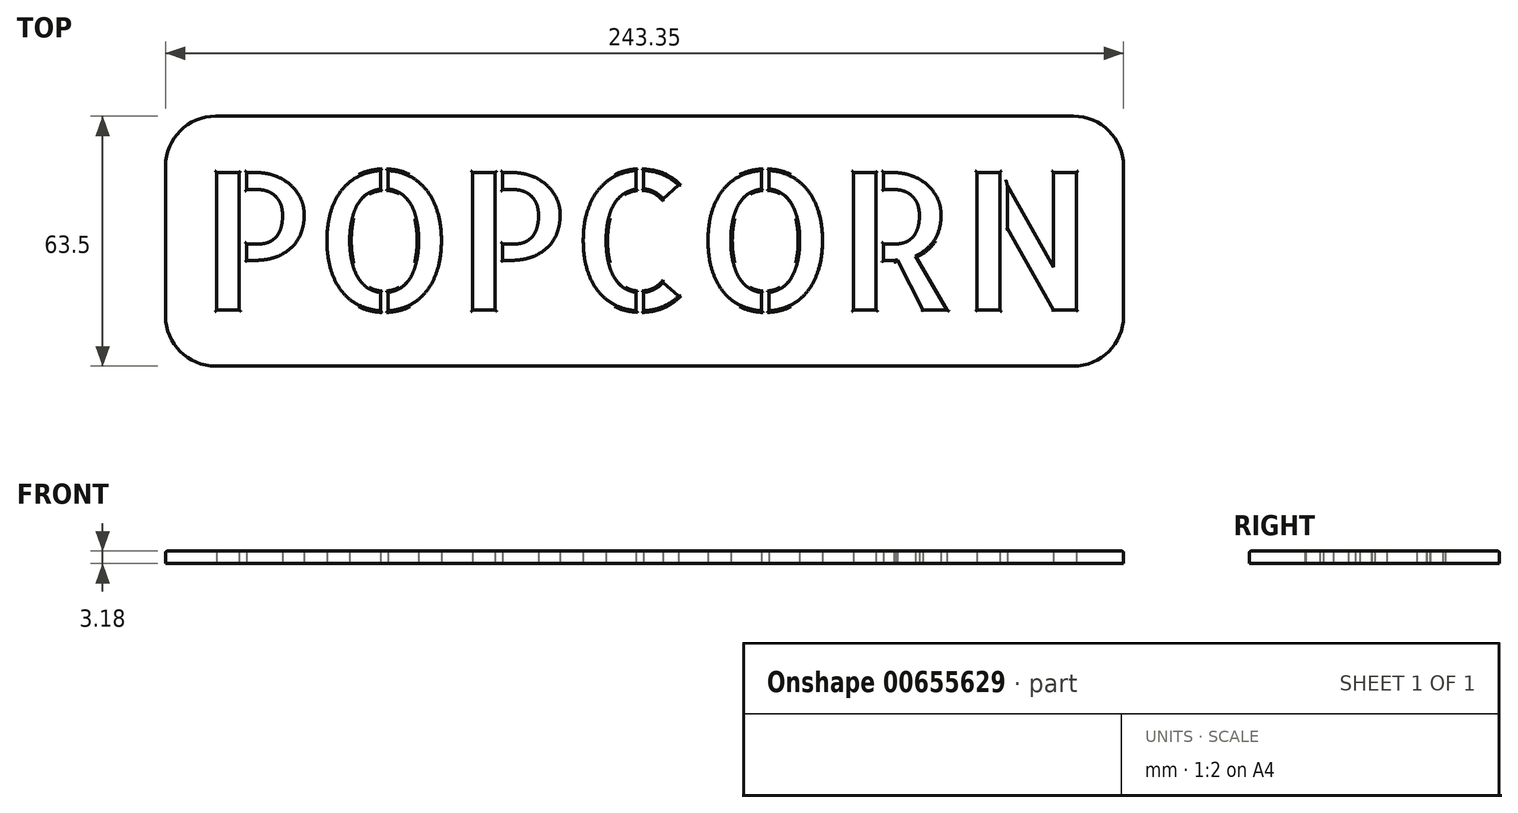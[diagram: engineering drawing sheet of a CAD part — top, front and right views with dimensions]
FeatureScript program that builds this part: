
annotation { "Feature Type Name" : "Feature", "Feature Type Description" : "" }
export const myFeature = defineFeature(function(context is Context, id is Id, definition is map)
    precondition{}
    {
        {
            var Q0;
            Q0=qCreatedBy(makeId("Top.planeOp"),FACE);
            var sketch = newSketch(context, id + "F0", { "sketchPlane" : qUnion([Q0])});
            skLineSegment(sketch, "E0.bottom", {"start": v(12.7, 0) * mm, "end": v(230.65, 0) * mm});
            skLineSegment(sketch, "E0.top", {"start": v(12.7, 63.5) * mm, "end": v(230.65, 63.5) * mm});
            skLineSegment(sketch, "E0.left", {"start": v(0, 12.7) * mm, "end": v(0, 50.8) * mm});
            skLineSegment(sketch, "E0.right", {"start": v(243.35, 12.7) * mm, "end": v(243.35, 50.8) * mm});
            skPoint(sketch, "E1.visualSharp", {"position": v(0, 63.5) * mm});
            skArc(sketch, "E1.filletArc", {"start": v(12.7, 63.5) * mm, "mid": v(3.72, 59.78) * mm, "end": v(0, 50.8) * mm});
            skPoint(sketch, "E2.visualSharp", {"position": v(0, 0) * mm});
            skArc(sketch, "E2.filletArc", {"start": v(0, 12.7) * mm, "mid": v(3.72, 3.72) * mm, "end": v(12.7, 0) * mm});
            skPoint(sketch, "E3.visualSharp", {"position": v(243.35, 0) * mm});
            skArc(sketch, "E3.filletArc", {"start": v(230.65, 0) * mm, "mid": v(239.63, 3.72) * mm, "end": v(243.35, 12.7) * mm});
            skPoint(sketch, "E4.visualSharp", {"position": v(243.35, 63.5) * mm});
            skArc(sketch, "E4.filletArc", {"start": v(243.35, 50.8) * mm, "mid": v(239.63, 59.78) * mm, "end": v(230.65, 63.5) * mm});
            skSolve(sketch);
        }
        {
            var Q0;
            Q0=qSketchRegion(id+"F0",true);
            extrude(context, id + "F1", {"entities" : qUnion([Q0]), "depth" : 3.17 * mm, "offsetDistance" : 25.4 * mm});
        }
        {
            var Q0;
            Q0=qCreatedBy(makeId("Top.planeOp"),FACE);
            var sketch = newSketch(context, id + "F2", { "sketchPlane" : qUnion([Q0])});
            skText(sketch, "E5", { "text": "POPCORN", "fontName": "AllertaStencil-Regular.ttf"});
            const initialGuessF2  = {"E5": [0.00869, 0.01429, 1, 0, 0.03492]};
            skSetInitialGuess(sketch, initialGuessF2);
            skSolve(sketch);
        }
        {
            var Q0;
            Q0=qSketchRegion(id+"F2",true);
            extrude(context, id + "F3", {"entities" : qUnion([Q0]), "operationType" : NewBodyOperationType.REMOVE, "endBound" : BoundingType.THROUGH_ALL, "depth" : 25.4 * mm, "offsetDistance" : 25.4 * mm});
        }
        {
            var Q0;
            Q0=makeQuery(id+"F1.opExtrude","CAP_FACE",FACE,{"disambiguationData":[OSD([sQuery(id+"F0.wireOp",EDGE,"E0.bottom"),sQuery(id+"F0.wireOp",EDGE,"E0.top"),sQuery(id+"F0.wireOp",EDGE,"E0.left"),sQuery(id+"F0.wireOp",EDGE,"E0.right"),sQuery(id+"F0.wireOp",EDGE,"E1.filletArc"),sQuery(id+"F0.wireOp",EDGE,"E2.filletArc"),sQuery(id+"F0.wireOp",EDGE,"E3.filletArc"),sQuery(id+"F0.wireOp",EDGE,"E4.filletArc")])],"isStart":false});
            fillet(context, id + "F4", {"entities" : qUnion([Q0]), "radius" : 0.38 * mm, "tangentPropagation" : true, "allowEdgeOverflow" : false});
        }
    });
